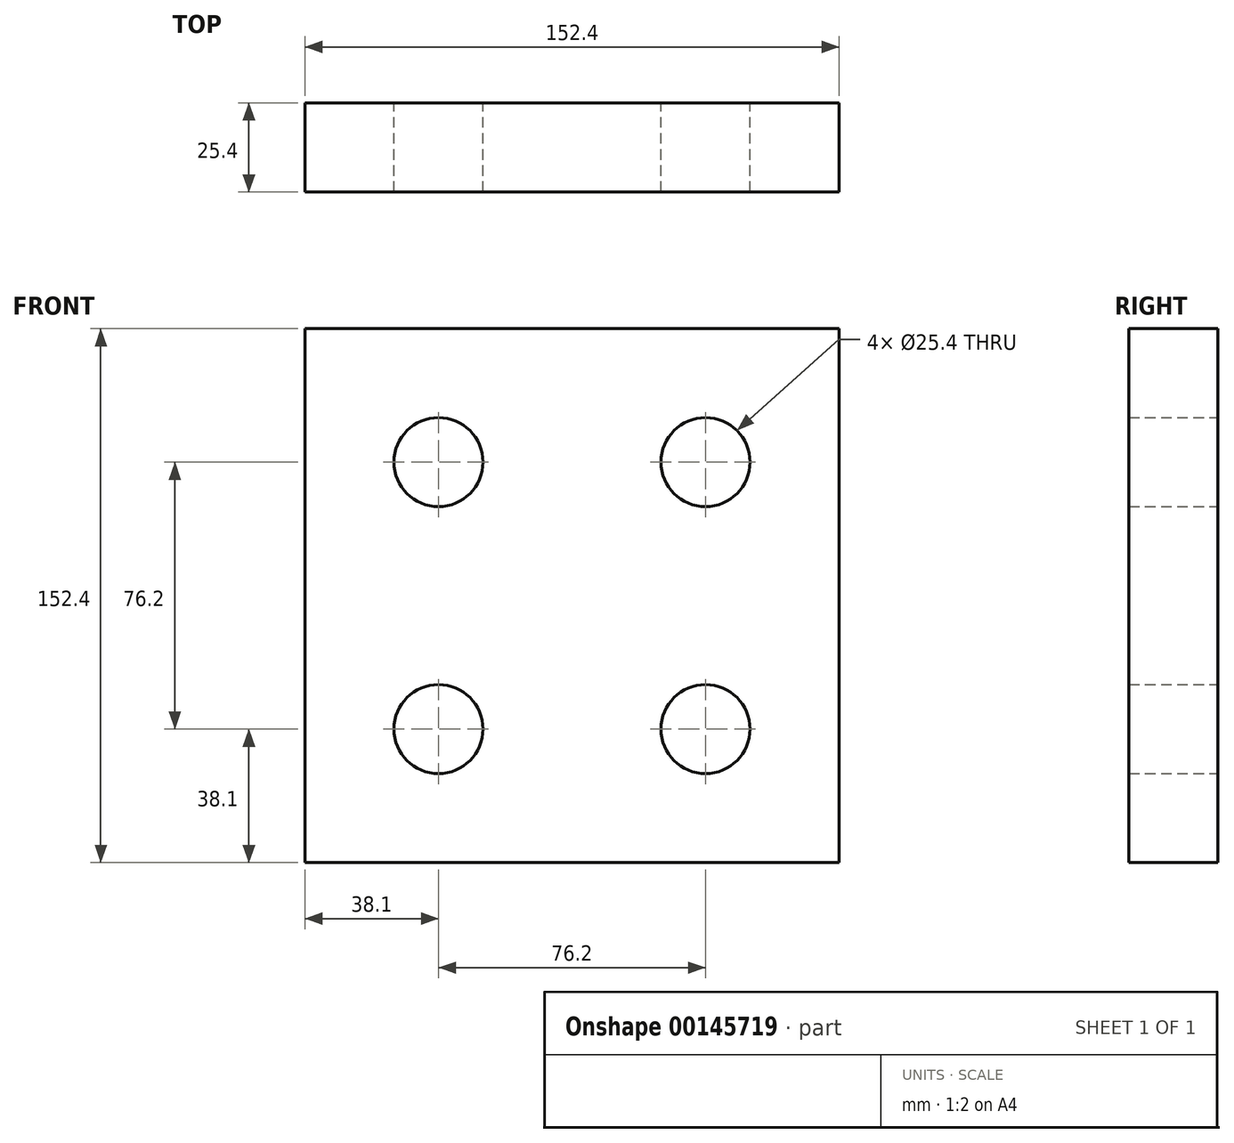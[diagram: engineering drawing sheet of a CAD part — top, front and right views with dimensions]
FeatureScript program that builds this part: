
annotation { "Feature Type Name" : "Feature", "Feature Type Description" : "" }
export const myFeature = defineFeature(function(context is Context, id is Id, definition is map)
    precondition{}
    {
        {
            var Q0;
            Q0=qCreatedBy(makeId("Front.planeOp"),FACE);
            var sketch = newSketch(context, id + "F0", { "sketchPlane" : qUnion([Q0])});
            skCircle(sketch, "E0", {"center": v(-38.1, 38.1) * mm, "radius": 12.7 * mm});
            skCircle(sketch, "E1", {"center": v(38.1, -38.1) * mm, "radius": 12.7 * mm});
            skCircle(sketch, "E2", {"center": v(-38.1, -38.1) * mm, "radius": 12.7 * mm});
            skCircle(sketch, "E3", {"center": v(38.1, 38.1) * mm, "radius": 12.7 * mm});
            skLineSegment(sketch, "E4", {"start": v(-38.1, 38.1) * mm, "end": v(38.1, 38.1) * mm, "construction": true});
            skLineSegment(sketch, "E5", {"start": v(38.1, -38.1) * mm, "end": v(38.1, 38.1) * mm, "construction": true});
            skLineSegment(sketch, "E6", {"start": v(38.1, -38.1) * mm, "end": v(-38.1, -38.1) * mm, "construction": true});
            skLineSegment(sketch, "E7", {"start": v(-38.1, 38.1) * mm, "end": v(-38.1, -38.1) * mm, "construction": true});
            skLineSegment(sketch, "E8", {"start": v(0, 38.1) * mm, "end": v(0, 0) * mm, "construction": true});
            skLineSegment(sketch, "E9", {"start": v(0, 0) * mm, "end": v(-38.1, 0) * mm, "construction": true});
            skLineSegment(sketch, "E10.bottom", {"start": v(-76.2, 76.2) * mm, "end": v(76.2, 76.2) * mm});
            skLineSegment(sketch, "E10.top", {"start": v(-76.2, -76.2) * mm, "end": v(76.2, -76.2) * mm});
            skLineSegment(sketch, "E10.left", {"start": v(-76.2, 76.2) * mm, "end": v(-76.2, -76.2) * mm});
            skLineSegment(sketch, "E10.right", {"start": v(76.2, 76.2) * mm, "end": v(76.2, -76.2) * mm});
            skLineSegment(sketch, "E11", {"start": v(0, 0) * mm, "end": v(-76.2, 76.2) * mm, "construction": true});
            skLineSegment(sketch, "E12", {"start": v(0, 0) * mm, "end": v(76.2, -76.2) * mm, "construction": true});
            skSolve(sketch);
        }
        {
            var Q0;
            Q0 = qSketchRegion(id + "F0", true);
            extrude(context, id + "F1", {"entities" : qUnion([Q0]), "depth" : 25.4 * mm});
        }
    });
